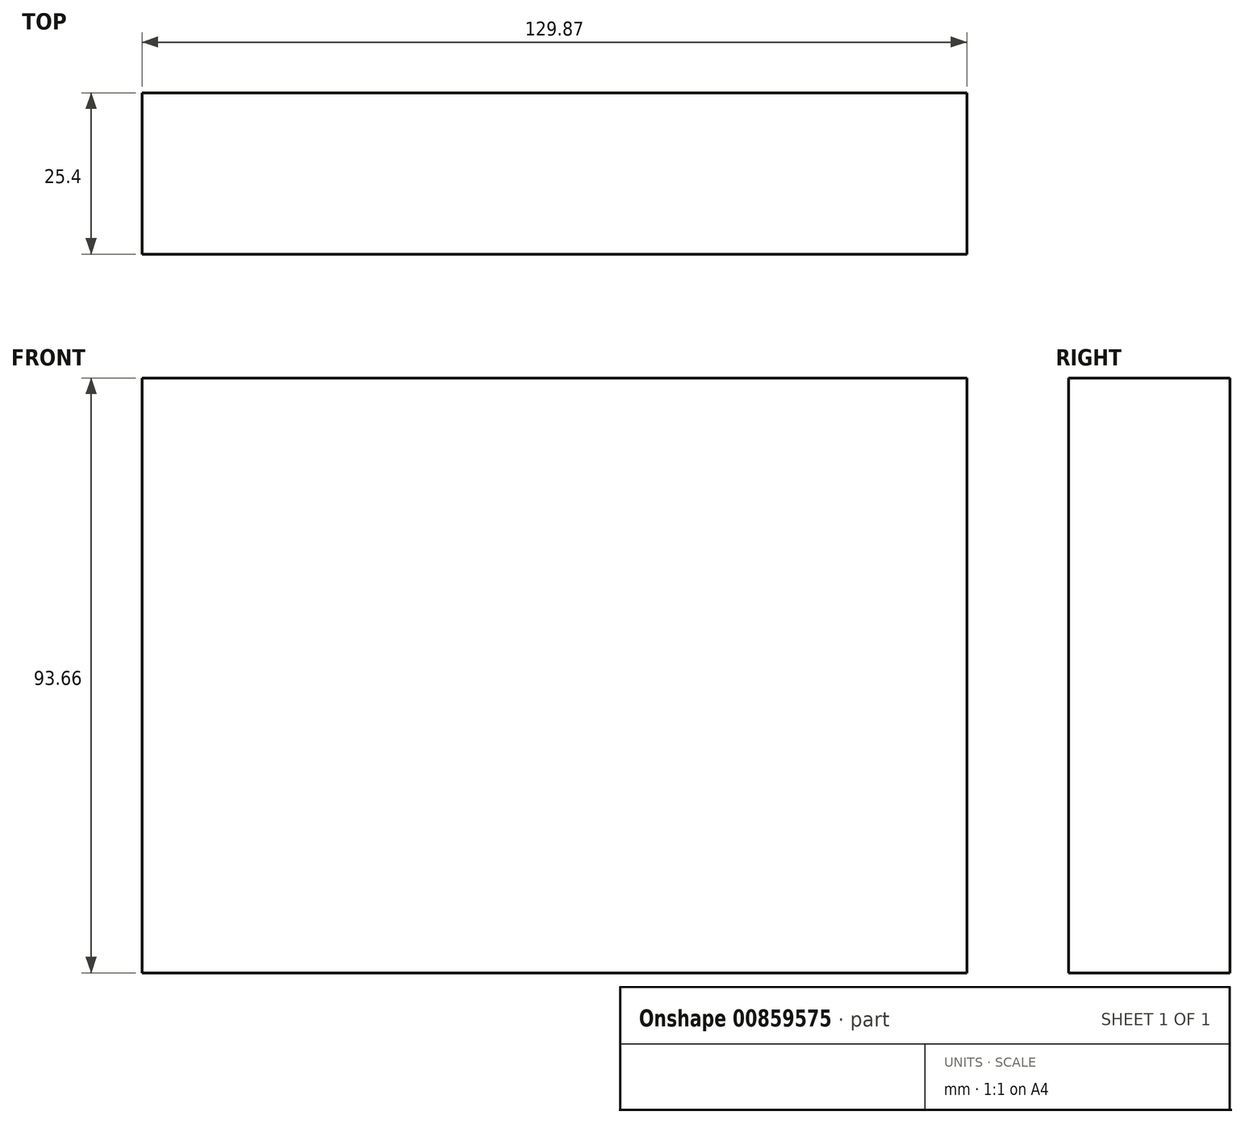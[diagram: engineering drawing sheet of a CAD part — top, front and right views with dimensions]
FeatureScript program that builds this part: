
annotation { "Feature Type Name" : "Feature", "Feature Type Description" : "" }
export const myFeature = defineFeature(function(context is Context, id is Id, definition is map)
    precondition{}
    {
        {
            var Q0;
            Q0=qCreatedBy(makeId("Front.planeOp"),FACE);
            var sketch = newSketch(context, id + "F0", { "sketchPlane" : qUnion([Q0])});
            skLineSegment(sketch, "E0.bottom", {"start": v(-62.66, 47.5) * mm, "end": v(67.21, 47.5) * mm});
            skLineSegment(sketch, "E0.top", {"start": v(-62.66, -46.17) * mm, "end": v(67.21, -46.17) * mm});
            skLineSegment(sketch, "E0.left", {"start": v(-62.66, 47.5) * mm, "end": v(-62.66, -46.17) * mm});
            skLineSegment(sketch, "E0.right", {"start": v(67.21, 47.5) * mm, "end": v(67.21, -46.17) * mm});
            skSolve(sketch);
        }
        {
            var Q0;
            Q0 = qSketchRegion(id + "F0", true);
            extrude(context, id + "F1", {"entities" : qUnion([Q0]), "depth" : 25.4 * mm, "offsetDistance" : 25.4 * mm});
        }
    });
